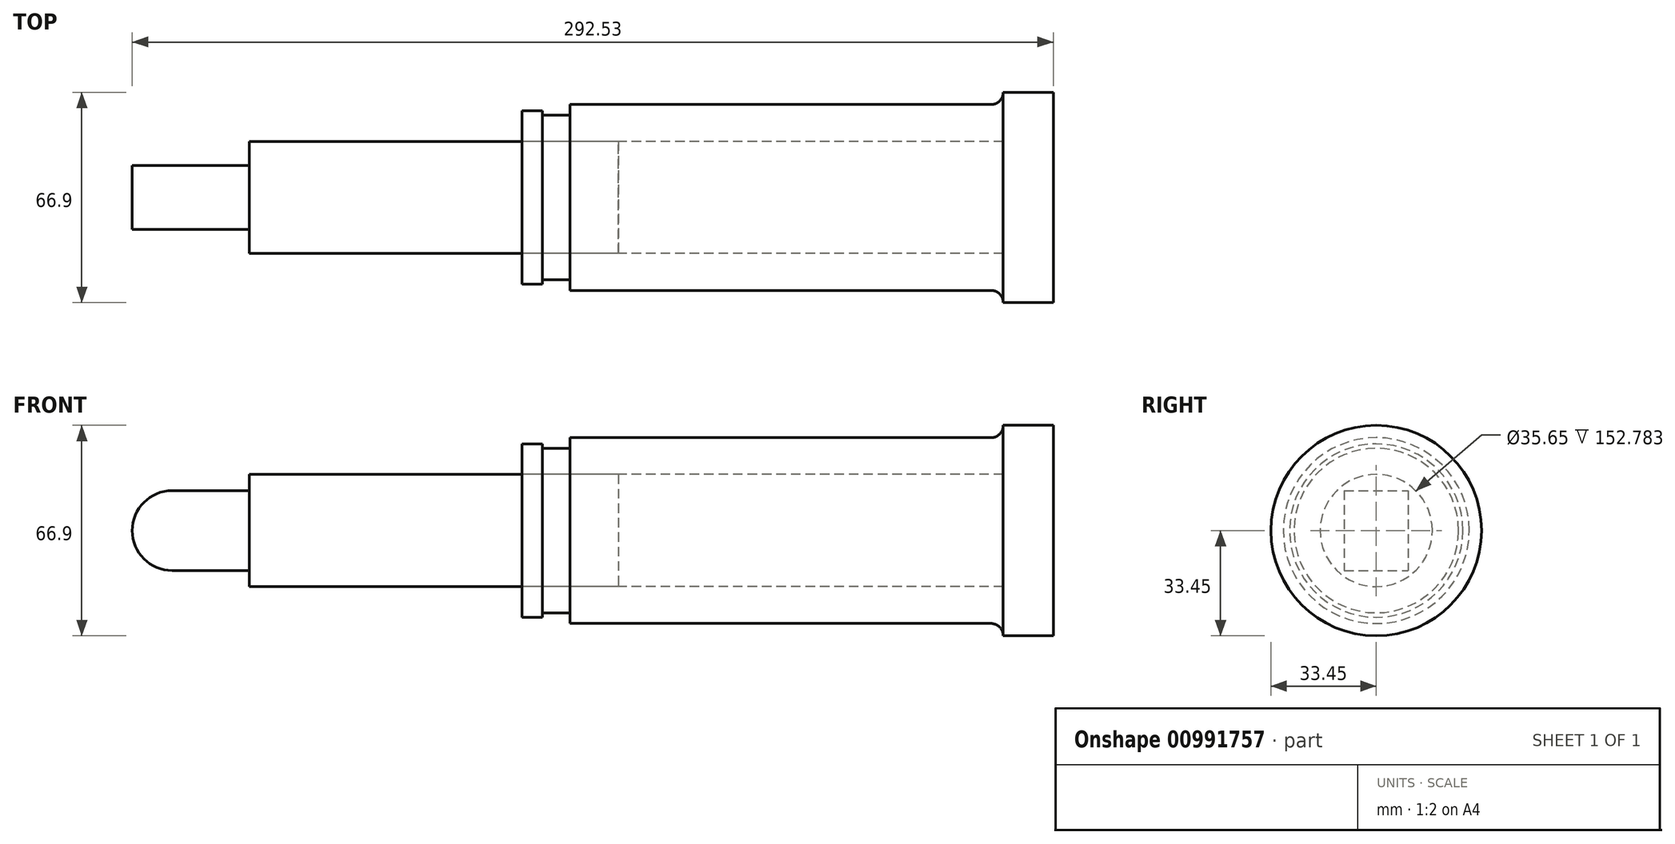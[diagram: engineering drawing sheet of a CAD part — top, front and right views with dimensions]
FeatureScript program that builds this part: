
annotation { "Feature Type Name" : "Feature", "Feature Type Description" : "" }
export const myFeature = defineFeature(function(context is Context, id is Id, definition is map)
    precondition{}
    {
        {
            var Q0;
            Q0=qCreatedBy(makeId("Front.planeOp"),FACE);
            var sketch = newSketch(context, id + "F0", { "sketchPlane" : qUnion([Q0])});
            skCircle(sketch, "E0", {"center": v(0, 0) * mm, "radius": 12.7 * mm});
            skLineSegment(sketch, "E1", {"start": v(0, 0) * mm, "end": v(24.48, 0) * mm});
            skLineSegment(sketch, "E2", {"start": v(24.48, 0) * mm, "end": v(279.83, 0) * mm});
            skLineSegment(sketch, "E3", {"start": v(279.83, 0) * mm, "end": v(279.83, 33.45) * mm});
            skLineSegment(sketch, "E4", {"start": v(279.83, 33.45) * mm, "end": v(263.92, 33.45) * mm});
            skLineSegment(sketch, "E5", {"start": v(263.92, 33.45) * mm, "end": v(263.92, 33.45) * mm});
            skLineSegment(sketch, "E6", {"start": v(260, 29.54) * mm, "end": v(126.28, 29.54) * mm});
            skLineSegment(sketch, "E7", {"start": v(126.28, 29.54) * mm, "end": v(126.28, 26.14) * mm});
            skLineSegment(sketch, "E8", {"start": v(126.28, 26.14) * mm, "end": v(117.59, 26.14) * mm});
            skLineSegment(sketch, "E9", {"start": v(117.59, 26.14) * mm, "end": v(117.59, 27.54) * mm});
            skLineSegment(sketch, "E10", {"start": v(117.59, 27.54) * mm, "end": v(111.14, 27.54) * mm});
            skLineSegment(sketch, "E11", {"start": v(111.14, 27.54) * mm, "end": v(111.14, 26.14) * mm});
            skLineSegment(sketch, "E12", {"start": v(111.14, 26.14) * mm, "end": v(111.14, 17.83) * mm});
            skLineSegment(sketch, "E13", {"start": v(111.14, 17.83) * mm, "end": v(24.48, 17.83) * mm});
            skLineSegment(sketch, "E14", {"start": v(24.48, 17.83) * mm, "end": v(24.48, 12.7) * mm});
            skLineSegment(sketch, "E15", {"start": v(24.48, 12.7) * mm, "end": v(0, 12.7) * mm});
            skLineSegment(sketch, "E16", {"start": v(0, 12.7) * mm, "end": v(0, 0) * mm});
            skLineSegment(sketch, "E17", {"start": v(0, -12.7) * mm, "end": v(24.48, -12.7) * mm});
            skLineSegment(sketch, "E18", {"start": v(24.48, -12.7) * mm, "end": v(24.48, 0) * mm});
            skLineSegment(sketch, "E19", {"start": v(24.48, 12.7) * mm, "end": v(24.48, 0) * mm});
            skLineSegment(sketch, "E20", {"start": v(0, 0) * mm, "end": v(0, -12.7) * mm});
            skLineSegment(sketch, "E21", {"start": v(111.14, 17.83) * mm, "end": v(263.92, 17.83) * mm});
            skLineSegment(sketch, "E22", {"start": v(263.92, 17.83) * mm, "end": v(263.92, 0) * mm});
            skLineSegment(sketch, "E23", {"start": v(111.14, 17.83) * mm, "end": v(111.14, 0) * mm});
            skLineSegment(sketch, "E24", {"start": v(141.65, 17.83) * mm, "end": v(141.65, 0) * mm});
            skPoint(sketch, "E25.visualSharp", {"position": v(263.92, 29.54) * mm});
            skArc(sketch, "E25.filletArc", {"start": v(260, 29.54) * mm, "mid": v(262.78, 30.68) * mm, "end": v(263.92, 33.45) * mm});
            skCircle(sketch, "E26", {"center": v(303.29, 0) * mm, "radius": 10.31 * mm});
            skLineSegment(sketch, "E27", {"start": v(279.83, 0) * mm, "end": v(303.29, 0) * mm, "construction": true});
            skLineSegment(sketch, "E28", {"start": v(303.29, 10.31) * mm, "end": v(279.83, 10.31) * mm});
            skLineSegment(sketch, "E29", {"start": v(303.84, -10.3) * mm, "end": v(279.83, -10.3) * mm});
            skLineSegment(sketch, "E30", {"start": v(279.83, -10.3) * mm, "end": v(279.83, 0) * mm});
            skLineSegment(sketch, "E31", {"start": v(-12.7, 0) * mm, "end": v(-47.14, 0) * mm, "construction": true});
            skSolve(sketch);
        }
        {
            var Q0;
            {var subQ5=sQuery(id+"F0.wireOp",EDGE,"E4");Q0=makeQuery(id+"F0.imprint","IMPRINT",FACE,{"disambiguationData":[TD([[makeQuery(id+"F0.imprint","IMPRINT",EDGE,{"derivedFrom":subQ5}),1.0]])]});}
            var Q1;
            Q1=sQuery(id+"F0.wireOp",EDGE,"E2");
            revolve(context, id + "F1", {"surfaceOperationType" : NewSurfaceOperationType.NEW, "entities" : qUnion([Q0]), "axis" : qUnion([Q1]), "revolveType" : RevolveType.FULL});
        }
        {
            var Q0;
            Q0=makeQuery(id+"F0.imprint","IMPRINT",FACE,{"disambiguationData":[TD([[makeQuery(id+"F0.imprint","IMPRINT",EDGE,{"derivedFrom":sQuery(id+"F0.wireOp",EDGE,"E13")}),1.0]])]});
            var Q1;
            {var subQ0=sQuery(id+"F0.wireOp",EDGE,"E23");Q1=makeQuery(id+"F0.imprint","IMPRINT",FACE,{"disambiguationData":[TD([[makeQuery(id+"F0.imprint","IMPRINT",EDGE,{"derivedFrom":subQ0}),1.0]])]});}
            var Q2;
            Q2=sQuery(id+"F0.wireOp",EDGE,"E2");
            revolve(context, id + "F2", {"surfaceOperationType" : NewSurfaceOperationType.NEW, "entities" : qUnion([Q0, Q1]), "axis" : qUnion([Q2]), "revolveType" : RevolveType.FULL});
        }
        {
            var Q0;
            {var subQ0=sQuery(id+"F0.wireOp",EDGE,"E15");Q0=makeQuery(id+"F0.imprint","IMPRINT",FACE,{"disambiguationData":[TD([[makeQuery(id+"F0.imprint","IMPRINT",EDGE,{"derivedFrom":subQ0}),1.0]])]});}
            var Q1;
            {var subQ0=sQuery(id+"F0.wireOp",EDGE,"E17");Q1=makeQuery(id+"F0.imprint","IMPRINT",FACE,{"disambiguationData":[TD([[makeQuery(id+"F0.imprint","IMPRINT",EDGE,{"derivedFrom":subQ0}),1.0]])]});}
            var Q2;
            {var subQ0=sQuery(id+"F0.wireOp",EDGE,"E16");Q2=makeQuery(id+"F0.imprint","IMPRINT",FACE,{"disambiguationData":[TD([[makeQuery(id+"F0.imprint","IMPRINT",EDGE,{"derivedFrom":subQ0}),1.0]])]});}
            var Q3;
            {var subQ0=sQuery(id+"F0.wireOp",EDGE,"E20");Q3=makeQuery(id+"F0.imprint","IMPRINT",FACE,{"disambiguationData":[TD([[makeQuery(id+"F0.imprint","IMPRINT",EDGE,{"derivedFrom":subQ0}),1.0]])]});}
            var Q4;
            {var subQ0=sQuery(id+"F0.wireOp",EDGE,"E16");Q4=makeQuery(id+"F0.imprint","IMPRINT",FACE,{"disambiguationData":[TD([[makeQuery(id+"F0.imprint","IMPRINT",EDGE,{"derivedFrom":subQ0}),-1.0]])]});}
            extrude(context, id + "F3", {"entities" : qUnion([Q0, Q1, Q2, Q3, Q4]), "operationType" : NewBodyOperationType.ADD, "endBound" : BoundingType.SYMMETRIC, "depth" : 20.32 * mm, "offsetDistance" : 25.4 * mm});
        }
    });
